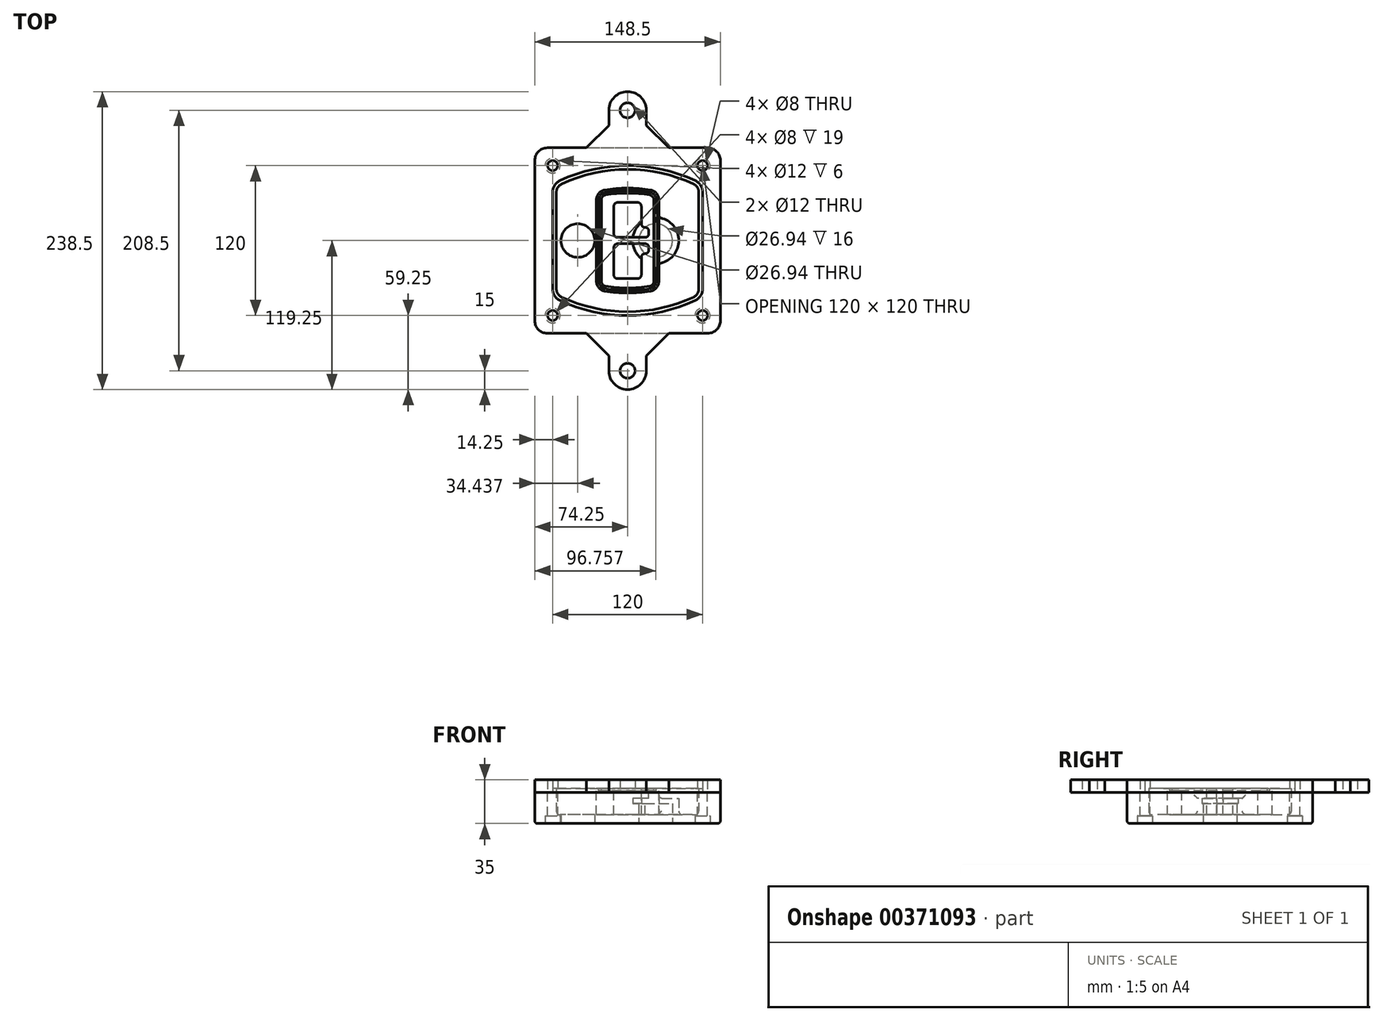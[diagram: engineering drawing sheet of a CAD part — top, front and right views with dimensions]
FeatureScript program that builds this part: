
annotation { "Feature Type Name" : "Feature", "Feature Type Description" : "" }
export const myFeature = defineFeature(function(context is Context, id is Id, definition is map)
    precondition{}
    {
        {
            var Q0;
            Q0=qCreatedBy(makeId("Top.planeOp"),FACE);
            var sketch = newSketch(context, id + "F0", { "sketchPlane" : qUnion([Q0])});
            skPoint(sketch, "E0.rect.middle", {"position": v(0, 0) * mm});
            skLineSegment(sketch, "E1.bottom", {"start": v(-64.25, -74.25) * mm, "end": v(64.25, -74.25) * mm});
            skLineSegment(sketch, "E1.top", {"start": v(-64.25, 74.25) * mm, "end": v(64.25, 74.25) * mm});
            skLineSegment(sketch, "E1.left", {"start": v(-74.25, -64.25) * mm, "end": v(-74.25, 64.25) * mm});
            skLineSegment(sketch, "E1.right", {"start": v(74.25, -64.25) * mm, "end": v(74.25, 64.25) * mm});
            skLineSegment(sketch, "E2", {"start": v(-74.25, 74.25) * mm, "end": v(74.25, -74.25) * mm, "construction": true});
            skLineSegment(sketch, "E3", {"start": v(74.25, 74.25) * mm, "end": v(-74.25, -74.25) * mm, "construction": true});
            skCircle(sketch, "E4", {"center": v(-60, 60) * mm, "radius": 4 * mm});
            skCircle(sketch, "E5", {"center": v(60, 60) * mm, "radius": 4 * mm});
            skCircle(sketch, "E6", {"center": v(60, -60) * mm, "radius": 4 * mm});
            skCircle(sketch, "E7", {"center": v(-60, -60) * mm, "radius": 4 * mm});
            skLineSegment(sketch, "E8", {"start": v(-60, 60) * mm, "end": v(60, 60) * mm, "construction": true});
            skLineSegment(sketch, "E9", {"start": v(60, 60) * mm, "end": v(60, -60) * mm, "construction": true});
            skLineSegment(sketch, "E10", {"start": v(60, -60) * mm, "end": v(-60, -60) * mm, "construction": true});
            skLineSegment(sketch, "E11", {"start": v(-60, -60) * mm, "end": v(-60, 60) * mm, "construction": true});
            skLineSegment(sketch, "E12", {"start": v(-60, 38.83) * mm, "end": v(-60, -38.83) * mm});
            skLineSegment(sketch, "E13", {"start": v(60, 38.83) * mm, "end": v(60, -38.83) * mm});
            skArc(sketch, "E14", {"start": v(54.26, 47.88) * mm, "mid": v(0, 60) * mm, "end": v(-54.26, 47.88) * mm});
            skArc(sketch, "E15", {"start": v(-54.26, -47.88) * mm, "mid": v(0, -60) * mm, "end": v(54.26, -47.88) * mm});
            skLineSegment(sketch, "E16", {"start": v(-60, 0) * mm, "end": v(60, 0) * mm, "construction": true});
            skPoint(sketch, "E17.visualSharp", {"position": v(-60, -45) * mm});
            skArc(sketch, "E17.filletArc", {"start": v(-60, -38.83) * mm, "mid": v(-58.44, -44.2) * mm, "end": v(-54.26, -47.88) * mm});
            skPoint(sketch, "E18.visualSharp", {"position": v(-60, 45) * mm});
            skArc(sketch, "E18.filletArc", {"start": v(-54.26, 47.88) * mm, "mid": v(-58.44, 44.2) * mm, "end": v(-60, 38.83) * mm});
            skPoint(sketch, "E19.visualSharp", {"position": v(60, 45) * mm});
            skArc(sketch, "E19.filletArc", {"start": v(60, 38.83) * mm, "mid": v(58.44, 44.2) * mm, "end": v(54.26, 47.88) * mm});
            skPoint(sketch, "E20.visualSharp", {"position": v(60, -45) * mm});
            skArc(sketch, "E20.filletArc", {"start": v(54.26, -47.88) * mm, "mid": v(58.44, -44.2) * mm, "end": v(60, -38.83) * mm});
            skPoint(sketch, "E21.visualSharp", {"position": v(-74.25, 74.25) * mm});
            skArc(sketch, "E21.filletArc", {"start": v(-64.25, 74.25) * mm, "mid": v(-71.32, 71.32) * mm, "end": v(-74.25, 64.25) * mm});
            skPoint(sketch, "E22.visualSharp", {"position": v(74.25, 74.25) * mm});
            skArc(sketch, "E22.filletArc", {"start": v(74.25, 64.25) * mm, "mid": v(71.32, 71.32) * mm, "end": v(64.25, 74.25) * mm});
            skPoint(sketch, "E23.visualSharp", {"position": v(74.25, -74.25) * mm});
            skArc(sketch, "E23.filletArc", {"start": v(64.25, -74.25) * mm, "mid": v(71.32, -71.32) * mm, "end": v(74.25, -64.25) * mm});
            skPoint(sketch, "E24.visualSharp", {"position": v(-74.25, -74.25) * mm});
            skArc(sketch, "E24.filletArc", {"start": v(-74.25, -64.25) * mm, "mid": v(-71.32, -71.32) * mm, "end": v(-64.25, -74.25) * mm});
            skArc(sketch, "E25.0", {"start": v(57, 38.83) * mm, "mid": v(55.9, 42.58) * mm, "end": v(52.98, 45.17) * mm});
            skLineSegment(sketch, "E25.1", {"start": v(57, 38.83) * mm, "end": v(57, -38.83) * mm});
            skArc(sketch, "E25.2", {"start": v(52.98, -45.17) * mm, "mid": v(55.9, -42.58) * mm, "end": v(57, -38.83) * mm});
            skArc(sketch, "E25.3", {"start": v(-52.98, -45.17) * mm, "mid": v(0, -57) * mm, "end": v(52.98, -45.17) * mm});
            skArc(sketch, "E25.4", {"start": v(-57, -38.83) * mm, "mid": v(-55.9, -42.58) * mm, "end": v(-52.98, -45.17) * mm});
            skArc(sketch, "E25.5", {"start": v(52.98, 45.17) * mm, "mid": v(0, 57) * mm, "end": v(-52.98, 45.17) * mm});
            skLineSegment(sketch, "E25.6", {"start": v(-57, 38.83) * mm, "end": v(-57, -38.83) * mm});
            skArc(sketch, "E25.7", {"start": v(-52.98, 45.17) * mm, "mid": v(-55.9, 42.58) * mm, "end": v(-57, 38.83) * mm});
            skArc(sketch, "E26.0", {"start": v(-55.96, 51.5) * mm, "mid": v(-61.82, 46.33) * mm, "end": v(-64, 38.83) * mm});
            skArc(sketch, "E26.1", {"start": v(55.96, 51.5) * mm, "mid": v(0, 64) * mm, "end": v(-55.96, 51.5) * mm});
            skArc(sketch, "E26.2", {"start": v(64, 38.83) * mm, "mid": v(61.82, 46.33) * mm, "end": v(55.96, 51.5) * mm});
            skLineSegment(sketch, "E26.3", {"start": v(64, 38.83) * mm, "end": v(64, -38.83) * mm});
            skArc(sketch, "E26.4", {"start": v(55.96, -51.5) * mm, "mid": v(61.82, -46.33) * mm, "end": v(64, -38.83) * mm});
            skLineSegment(sketch, "E26.5", {"start": v(-64, 38.83) * mm, "end": v(-64, -38.83) * mm});
            skArc(sketch, "E26.6", {"start": v(-55.96, -51.5) * mm, "mid": v(0, -64) * mm, "end": v(55.96, -51.5) * mm});
            skArc(sketch, "E26.7", {"start": v(-64, -38.83) * mm, "mid": v(-61.82, -46.33) * mm, "end": v(-55.96, -51.5) * mm});
            skSolve(sketch);
        }
        {
            var Q0;
            Q0=makeQuery(id+"F0.imprint","IMPRINT",FACE,{"disambiguationData":[TD([[makeQuery(id+"F0.imprint","IMPRINT",EDGE,{"derivedFrom":sQuery(id+"F0.wireOp",EDGE,"E1.bottom")}),1.0]])]});
            var Q1;
            Q1=makeQuery(id+"F0.imprint","IMPRINT",FACE,{"disambiguationData":[TD([[makeQuery(id+"F0.imprint","IMPRINT",EDGE,{"derivedFrom":sQuery(id+"F0.wireOp",EDGE,"E12")}),1.0]])]});
            var Q2;
            Q2=makeQuery(id+"F0.imprint","IMPRINT",FACE,{"disambiguationData":[TD([[makeQuery(id+"F0.imprint","IMPRINT",EDGE,{"derivedFrom":sQuery(id+"F0.wireOp",EDGE,"E25.0")}),1.0]])]});
            var Q3;
            Q3=makeQuery(id+"F0.imprint","IMPRINT",FACE,{"disambiguationData":[TD([[makeQuery(id+"F0.imprint","IMPRINT",EDGE,{"derivedFrom":sQuery(id+"F0.wireOp",EDGE,"E12")}),-1.0]])]});
            extrude(context, id + "F1", {"entities" : qUnion([Q0, Q1, Q2, Q3]), "oppositeDirection" : true, "depth" : 25 * mm});
        }
        {
            var Q0;
            Q0=makeQuery(id+"F0.imprint","IMPRINT",FACE,{"disambiguationData":[TD([[makeQuery(id+"F0.imprint","IMPRINT",EDGE,{"derivedFrom":sQuery(id+"F0.wireOp",EDGE,"E12")}),1.0]])]});
            extrude(context, id + "F2", {"entities" : qUnion([Q0]), "operationType" : NewBodyOperationType.ADD, "depth" : 3 * mm});
        }
        {
            var Q0;
            Q0=makeQuery(id+"F0.imprint","IMPRINT",FACE,{"disambiguationData":[TD([[makeQuery(id+"F0.imprint","IMPRINT",EDGE,{"derivedFrom":sQuery(id+"F0.wireOp",EDGE,"E25.0")}),1.0]])]});
            extrude(context, id + "F3", {"entities" : qUnion([Q0]), "operationType" : NewBodyOperationType.REMOVE, "oppositeDirection" : true, "depth" : 18 * mm});
        }
        {
            var Q0;
            Q0=makeQuery(id+"F2.opExtrude","CAP_FACE",FACE,{"disambiguationData":[OSD([sQuery(id+"F0.wireOp",EDGE,"E12"),sQuery(id+"F0.wireOp",EDGE,"E13"),sQuery(id+"F0.wireOp",EDGE,"E14"),sQuery(id+"F0.wireOp",EDGE,"E15"),sQuery(id+"F0.wireOp",EDGE,"E17.filletArc"),sQuery(id+"F0.wireOp",EDGE,"E18.filletArc"),sQuery(id+"F0.wireOp",EDGE,"E19.filletArc"),sQuery(id+"F0.wireOp",EDGE,"E20.filletArc"),sQuery(id+"F0.wireOp",EDGE,"E25.0"),sQuery(id+"F0.wireOp",EDGE,"E25.1"),sQuery(id+"F0.wireOp",EDGE,"E25.2"),sQuery(id+"F0.wireOp",EDGE,"E25.3"),sQuery(id+"F0.wireOp",EDGE,"E25.4"),sQuery(id+"F0.wireOp",EDGE,"E25.5"),sQuery(id+"F0.wireOp",EDGE,"E25.6"),sQuery(id+"F0.wireOp",EDGE,"E25.7")])],"isStart":false});
            var sketch = newSketch(context, id + "F4", { "sketchPlane" : qUnion([Q0])});
            skArc(sketch, "E27.0", {"start": v(-18.34, -40.45) * mm, "mid": v(0, -42) * mm, "end": v(18.34, -40.45) * mm});
            skArc(sketch, "E28.0", {"start": v(18.34, 40.45) * mm, "mid": v(0, 42) * mm, "end": v(-18.34, 40.45) * mm});
            skLineSegment(sketch, "E29", {"start": v(-25, 32.57) * mm, "end": v(-25, -32.57) * mm});
            skLineSegment(sketch, "E30", {"start": v(25, 32.57) * mm, "end": v(25, -32.57) * mm});
            skLineSegment(sketch, "E31", {"start": v(-25, 39.1) * mm, "end": v(25, 39.1) * mm, "construction": true});
            skLineSegment(sketch, "E32", {"start": v(-25, -39.1) * mm, "end": v(25, -39.1) * mm, "construction": true});
            skPoint(sketch, "E33.visualSharp", {"position": v(-25, 39.1) * mm});
            skArc(sketch, "E33.filletArc", {"start": v(-18.34, 40.45) * mm, "mid": v(-23.11, 37.73) * mm, "end": v(-25, 32.57) * mm});
            skPoint(sketch, "E34.visualSharp", {"position": v(25, 39.1) * mm});
            skArc(sketch, "E34.filletArc", {"start": v(25, 32.57) * mm, "mid": v(23.11, 37.73) * mm, "end": v(18.34, 40.45) * mm});
            skPoint(sketch, "E35.visualSharp", {"position": v(25, -39.1) * mm});
            skArc(sketch, "E35.filletArc", {"start": v(18.34, -40.45) * mm, "mid": v(23.11, -37.73) * mm, "end": v(25, -32.57) * mm});
            skPoint(sketch, "E36.visualSharp", {"position": v(-25, -39.1) * mm});
            skArc(sketch, "E36.filletArc", {"start": v(-25, -32.57) * mm, "mid": v(-23.11, -37.73) * mm, "end": v(-18.34, -40.45) * mm});
            skArc(sketch, "E37.0", {"start": v(52.98, 45.17) * mm, "mid": v(0, 57) * mm, "end": v(-52.98, 45.17) * mm});
            skArc(sketch, "E37.1", {"start": v(-52.98, 45.17) * mm, "mid": v(-55.9, 42.58) * mm, "end": v(-57, 38.83) * mm});
            skLineSegment(sketch, "E37.2", {"start": v(-57, 38.83) * mm, "end": v(-57, -38.83) * mm});
            skArc(sketch, "E37.3", {"start": v(-57, -38.83) * mm, "mid": v(-55.9, -42.58) * mm, "end": v(-52.98, -45.17) * mm});
            skArc(sketch, "E37.4", {"start": v(-52.98, -45.17) * mm, "mid": v(0, -57) * mm, "end": v(52.98, -45.17) * mm});
            skArc(sketch, "E37.5", {"start": v(52.98, -45.17) * mm, "mid": v(55.9, -42.58) * mm, "end": v(57, -38.83) * mm});
            skLineSegment(sketch, "E37.6", {"start": v(57, 38.83) * mm, "end": v(57, -38.83) * mm});
            skArc(sketch, "E37.7", {"start": v(57, 38.83) * mm, "mid": v(55.9, 42.58) * mm, "end": v(52.98, 45.17) * mm});
            skLineSegment(sketch, "E38.0", {"start": v(23, 32.57) * mm, "end": v(23, -32.57) * mm});
            skArc(sketch, "E38.1", {"start": v(18, -38.48) * mm, "mid": v(21.58, -36.44) * mm, "end": v(23, -32.57) * mm});
            skArc(sketch, "E38.2", {"start": v(-18, -38.48) * mm, "mid": v(0, -40) * mm, "end": v(18, -38.48) * mm});
            skArc(sketch, "E38.3", {"start": v(-23, -32.57) * mm, "mid": v(-21.58, -36.44) * mm, "end": v(-18, -38.48) * mm});
            skLineSegment(sketch, "E38.4", {"start": v(-23, 32.57) * mm, "end": v(-23, -32.57) * mm});
            skArc(sketch, "E38.5", {"start": v(23, 32.57) * mm, "mid": v(21.58, 36.44) * mm, "end": v(18, 38.48) * mm});
            skArc(sketch, "E38.6", {"start": v(-18, 38.48) * mm, "mid": v(-21.58, 36.44) * mm, "end": v(-23, 32.57) * mm});
            skArc(sketch, "E38.7", {"start": v(18, 38.48) * mm, "mid": v(0, 40) * mm, "end": v(-18, 38.48) * mm});
            skArc(sketch, "E39.0", {"start": v(21, 32.57) * mm, "mid": v(20.06, 35.15) * mm, "end": v(17.67, 36.5) * mm});
            skLineSegment(sketch, "E39.1", {"start": v(21, 32.57) * mm, "end": v(21, -32.57) * mm});
            skArc(sketch, "E39.2", {"start": v(17.67, -36.5) * mm, "mid": v(20.06, -35.15) * mm, "end": v(21, -32.57) * mm});
            skArc(sketch, "E39.3", {"start": v(-17.67, -36.5) * mm, "mid": v(0, -38) * mm, "end": v(17.67, -36.5) * mm});
            skArc(sketch, "E39.4", {"start": v(-21, -32.57) * mm, "mid": v(-20.06, -35.15) * mm, "end": v(-17.67, -36.5) * mm});
            skArc(sketch, "E39.5", {"start": v(17.67, 36.5) * mm, "mid": v(0, 38) * mm, "end": v(-17.67, 36.5) * mm});
            skLineSegment(sketch, "E39.6", {"start": v(-21, 32.57) * mm, "end": v(-21, -32.57) * mm});
            skArc(sketch, "E39.7", {"start": v(-17.67, 36.5) * mm, "mid": v(-20.06, 35.15) * mm, "end": v(-21, 32.57) * mm});
            skLineSegment(sketch, "E40", {"start": v(-25, 0) * mm, "end": v(25, 0) * mm, "construction": true});
            skLineSegment(sketch, "E41", {"start": v(-11, 5.5) * mm, "end": v(-11, 27.5) * mm});
            skLineSegment(sketch, "E42", {"start": v(-8, 30.5) * mm, "end": v(8, 30.5) * mm});
            skLineSegment(sketch, "E43", {"start": v(11, 27.5) * mm, "end": v(11, 13.5) * mm});
            skLineSegment(sketch, "E44", {"start": v(14, 10.5) * mm, "end": v(14, 10.5) * mm});
            skLineSegment(sketch, "E45", {"start": v(17, 7.5) * mm, "end": v(17, 5.5) * mm});
            skLineSegment(sketch, "E46", {"start": v(14, 2.5) * mm, "end": v(-8, 2.5) * mm});
            skPoint(sketch, "E47.visualSharp", {"position": v(-11, 30.5) * mm});
            skArc(sketch, "E47.filletArc", {"start": v(-8, 30.5) * mm, "mid": v(-10.12, 29.62) * mm, "end": v(-11, 27.5) * mm});
            skPoint(sketch, "E48.visualSharp", {"position": v(11, 30.5) * mm});
            skArc(sketch, "E48.filletArc", {"start": v(11, 27.5) * mm, "mid": v(10.12, 29.62) * mm, "end": v(8, 30.5) * mm});
            skPoint(sketch, "E49.visualSharp", {"position": v(11, 10.5) * mm});
            skArc(sketch, "E49.filletArc", {"start": v(11, 13.5) * mm, "mid": v(11.88, 11.38) * mm, "end": v(14, 10.5) * mm});
            skPoint(sketch, "E50.visualSharp", {"position": v(17, 10.5) * mm});
            skArc(sketch, "E50.filletArc", {"start": v(17, 7.5) * mm, "mid": v(16.12, 9.62) * mm, "end": v(14, 10.5) * mm});
            skPoint(sketch, "E51.visualSharp", {"position": v(17, 2.5) * mm});
            skArc(sketch, "E51.filletArc", {"start": v(14, 2.5) * mm, "mid": v(16.12, 3.38) * mm, "end": v(17, 5.5) * mm});
            skPoint(sketch, "E52.visualSharp", {"position": v(-11, 2.5) * mm});
            skArc(sketch, "E52.filletArc", {"start": v(-11, 5.5) * mm, "mid": v(-10.12, 3.38) * mm, "end": v(-8, 2.5) * mm});
            skLineSegment(sketch, "E53.0.MirrorCS", {"start": v(14, -2.5) * mm, "end": v(-8, -2.5) * mm});
            skArc(sketch, "E54.0.MirrorCS", {"start": v(-11, -5.5) * mm, "mid": v(-10.12, -3.38) * mm, "end": v(-8, -2.5) * mm});
            skLineSegment(sketch, "E55.0.MirrorCS", {"start": v(-11, -5.5) * mm, "end": v(-11, -27.5) * mm});
            skArc(sketch, "E56.0.MirrorCS", {"start": v(-8, -30.5) * mm, "mid": v(-10.12, -29.62) * mm, "end": v(-11, -27.5) * mm});
            skLineSegment(sketch, "E57.0.MirrorCS", {"start": v(-8, -30.5) * mm, "end": v(8, -30.5) * mm});
            skArc(sketch, "E58.0.MirrorCS", {"start": v(11, -27.5) * mm, "mid": v(10.12, -29.62) * mm, "end": v(8, -30.5) * mm});
            skLineSegment(sketch, "E59.0.MirrorCS", {"start": v(11, -27.5) * mm, "end": v(11, -13.5) * mm});
            skArc(sketch, "E60.0.MirrorCS", {"start": v(11, -13.5) * mm, "mid": v(11.88, -11.38) * mm, "end": v(14, -10.5) * mm});
            skArc(sketch, "E61.0.MirrorCS", {"start": v(17, -7.5) * mm, "mid": v(16.12, -9.62) * mm, "end": v(14, -10.5) * mm});
            skLineSegment(sketch, "E62.0.MirrorCS", {"start": v(17, -7.5) * mm, "end": v(17, -5.5) * mm});
            skArc(sketch, "E63.0.MirrorCS", {"start": v(14, -2.5) * mm, "mid": v(16.12, -3.38) * mm, "end": v(17, -5.5) * mm});
            skSolve(sketch);
        }
        {
            var Q0;
            Q0=makeQuery(id+"F4.imprint","IMPRINT",FACE,{"disambiguationData":[TD([[makeQuery(id+"F4.imprint","IMPRINT",EDGE,{"derivedFrom":sQuery(id+"F4.wireOp",EDGE,"E27.0")}),1.0]])]});
            var Q1;
            Q1=makeQuery(id+"F4.imprint","IMPRINT",FACE,{"disambiguationData":[TD([[makeQuery(id+"F4.imprint","IMPRINT",EDGE,{"derivedFrom":sQuery(id+"F4.wireOp",EDGE,"E38.0")}),-1.0]])]});
            var Q2;
            Q2=makeQuery(id+"F4.imprint","IMPRINT",FACE,{"disambiguationData":[TD([[makeQuery(id+"F4.imprint","IMPRINT",EDGE,{"derivedFrom":sQuery(id+"F4.wireOp",EDGE,"E39.0")}),1.0]])]});
            extrude(context, id + "F5", {"entities" : qUnion([Q0, Q1, Q2]), "operationType" : NewBodyOperationType.ADD, "endBound" : BoundingType.UP_TO_NEXT, "oppositeDirection" : true, "depth" : 25 * mm});
        }
        {
            var Q0;
            Q0=makeQuery(id+"F4.imprint","IMPRINT",FACE,{"disambiguationData":[TD([[makeQuery(id+"F4.imprint","IMPRINT",EDGE,{"derivedFrom":sQuery(id+"F4.wireOp",EDGE,"E38.0")}),-1.0]])]});
            extrude(context, id + "F6", {"entities" : qUnion([Q0]), "operationType" : NewBodyOperationType.REMOVE, "oppositeDirection" : true, "depth" : 2 * mm});
        }
        {
            var Q0;
            Q0=makeQuery(id+"F1.opExtrude","CAP_FACE",FACE,{"disambiguationData":[OSD([sQuery(id+"F0.wireOp",EDGE,"E1.bottom"),sQuery(id+"F0.wireOp",EDGE,"E1.top"),sQuery(id+"F0.wireOp",EDGE,"E1.left"),sQuery(id+"F0.wireOp",EDGE,"E1.right"),sQuery(id+"F0.wireOp",EDGE,"E4"),sQuery(id+"F0.wireOp",EDGE,"E5"),sQuery(id+"F0.wireOp",EDGE,"E6"),sQuery(id+"F0.wireOp",EDGE,"E7"),sQuery(id+"F0.wireOp",EDGE,"E21.filletArc"),sQuery(id+"F0.wireOp",EDGE,"E22.filletArc"),sQuery(id+"F0.wireOp",EDGE,"E23.filletArc"),sQuery(id+"F0.wireOp",EDGE,"E24.filletArc")])],"isStart":false});
            var sketch = newSketch(context, id + "F7", { "sketchPlane" : qUnion([Q0])});
            skCircle(sketch, "E64", {"center": v(22.5, 0) * mm, "radius": 13.47 * mm});
            skCircle(sketch, "E65", {"center": v(-39.81, 0) * mm, "radius": 13.47 * mm});
            skLineSegment(sketch, "E66", {"start": v(74.25, 0) * mm, "end": v(-74.25, 0) * mm});
            skCircle(sketch, "E67", {"center": v(22.5, 0) * mm, "radius": 18.47 * mm});
            skCircle(sketch, "E68", {"center": v(60, -60) * mm, "radius": 6 * mm});
            skCircle(sketch, "E69", {"center": v(-60, -60) * mm, "radius": 6 * mm});
            skCircle(sketch, "E70", {"center": v(-60, 60) * mm, "radius": 6 * mm});
            skCircle(sketch, "E71", {"center": v(60, 60) * mm, "radius": 6 * mm});
            skSolve(sketch);
        }
        {
            var Q0;
            {var subQ1=sQuery(id+"F7.wireOp",EDGE,"E66");var subQ4=sQuery(id+"F7.wireOp",EDGE,"E64");var subQ6=makeQuery(id+"F7.imprint","INTERSECT",VERTEX,{"disambiguationData":[OD(0.0)],"derivedFrom":[subQ4,subQ1]});Q0=makeQuery(id+"F7.imprint","IMPRINT",FACE,{"disambiguationData":[TD([[makeQuery(id+"F7.imprint","IMPRINT",EDGE,{"disambiguationData":[TD([[subQ6,-1.0]])],"derivedFrom":subQ4}),-1.0]])]});}
            var Q1;
            {var subQ0=sQuery(id+"F7.wireOp",EDGE,"E66");var subQ1=sQuery(id+"F7.wireOp",EDGE,"E64");var subQ3=makeQuery(id+"F7.imprint","INTERSECT",VERTEX,{"disambiguationData":[OD(0.0)],"derivedFrom":[subQ1,subQ0]});Q1=makeQuery(id+"F7.imprint","IMPRINT",FACE,{"disambiguationData":[TD([[makeQuery(id+"F7.imprint","IMPRINT",EDGE,{"disambiguationData":[TD([[subQ3,-1.0]])],"derivedFrom":subQ1}),1.0]])]});}
            var Q2;
            {var subQ0=sQuery(id+"F7.wireOp",EDGE,"E66");var subQ1=sQuery(id+"F7.wireOp",EDGE,"E64");var subQ3=makeQuery(id+"F7.imprint","INTERSECT",VERTEX,{"disambiguationData":[OD(0.0)],"derivedFrom":[subQ1,subQ0]});Q2=makeQuery(id+"F7.imprint","IMPRINT",FACE,{"disambiguationData":[TD([[makeQuery(id+"F7.imprint","IMPRINT",EDGE,{"disambiguationData":[TD([[subQ3,1.0]])],"derivedFrom":subQ1}),1.0]])]});}
            var Q3;
            {var subQ1=sQuery(id+"F7.wireOp",EDGE,"E66");var subQ4=sQuery(id+"F7.wireOp",EDGE,"E64");var subQ6=makeQuery(id+"F7.imprint","INTERSECT",VERTEX,{"disambiguationData":[OD(0.0)],"derivedFrom":[subQ4,subQ1]});Q3=makeQuery(id+"F7.imprint","IMPRINT",FACE,{"disambiguationData":[TD([[makeQuery(id+"F7.imprint","IMPRINT",EDGE,{"disambiguationData":[TD([[subQ6,1.0]])],"derivedFrom":subQ4}),-1.0]])]});}
            extrude(context, id + "F8", {"entities" : qUnion([Q0, Q1, Q2, Q3]), "operationType" : NewBodyOperationType.ADD, "oppositeDirection" : true, "depth" : 20 * mm});
        }
        {
            var Q0;
            {var subQ0=sQuery(id+"F7.wireOp",EDGE,"E66");var subQ1=sQuery(id+"F7.wireOp",EDGE,"E64");var subQ3=makeQuery(id+"F7.imprint","INTERSECT",VERTEX,{"disambiguationData":[OD(0.0)],"derivedFrom":[subQ1,subQ0]});Q0=makeQuery(id+"F7.imprint","IMPRINT",FACE,{"disambiguationData":[TD([[makeQuery(id+"F7.imprint","IMPRINT",EDGE,{"disambiguationData":[TD([[subQ3,-1.0]])],"derivedFrom":subQ1}),1.0]])]});}
            var Q1;
            {var subQ0=sQuery(id+"F7.wireOp",EDGE,"E66");var subQ1=sQuery(id+"F7.wireOp",EDGE,"E64");var subQ3=makeQuery(id+"F7.imprint","INTERSECT",VERTEX,{"disambiguationData":[OD(0.0)],"derivedFrom":[subQ1,subQ0]});Q1=makeQuery(id+"F7.imprint","IMPRINT",FACE,{"disambiguationData":[TD([[makeQuery(id+"F7.imprint","IMPRINT",EDGE,{"disambiguationData":[TD([[subQ3,1.0]])],"derivedFrom":subQ1}),1.0]])]});}
            extrude(context, id + "F9", {"entities" : qUnion([Q0, Q1]), "operationType" : NewBodyOperationType.REMOVE, "oppositeDirection" : true, "depth" : 16 * mm});
        }
        {
            var Q0;
            {var subQ0=sQuery(id+"F7.wireOp",EDGE,"E66");var subQ1=sQuery(id+"F7.wireOp",EDGE,"E65");var subQ3=makeQuery(id+"F7.imprint","INTERSECT",VERTEX,{"disambiguationData":[OD(0.0)],"derivedFrom":[subQ1,subQ0]});Q0=makeQuery(id+"F7.imprint","IMPRINT",FACE,{"disambiguationData":[TD([[makeQuery(id+"F7.imprint","IMPRINT",EDGE,{"disambiguationData":[TD([[subQ3,-1.0]])],"derivedFrom":subQ1}),1.0]])]});}
            var Q1;
            {var subQ0=sQuery(id+"F7.wireOp",EDGE,"E66");var subQ1=sQuery(id+"F7.wireOp",EDGE,"E65");var subQ3=makeQuery(id+"F7.imprint","INTERSECT",VERTEX,{"disambiguationData":[OD(0.0)],"derivedFrom":[subQ1,subQ0]});Q1=makeQuery(id+"F7.imprint","IMPRINT",FACE,{"disambiguationData":[TD([[makeQuery(id+"F7.imprint","IMPRINT",EDGE,{"disambiguationData":[TD([[subQ3,1.0]])],"derivedFrom":subQ1}),1.0]])]});}
            extrude(context, id + "F10", {"entities" : qUnion([Q0, Q1]), "operationType" : NewBodyOperationType.REMOVE, "oppositeDirection" : true, "depth" : 25 * mm});
        }
        {
            var Q0;
            Q0=makeQuery(id+"F7.imprint","IMPRINT",FACE,{"disambiguationData":[TD([[makeQuery(id+"F7.imprint","IMPRINT",EDGE,{"derivedFrom":sQuery(id+"F7.wireOp",EDGE,"E68")}),1.0]])]});
            var Q1;
            Q1=makeQuery(id+"F7.imprint","IMPRINT",FACE,{"disambiguationData":[TD([[makeQuery(id+"F7.imprint","IMPRINT",EDGE,{"derivedFrom":makeQuery(id+"F1.opExtrude","CAP_EDGE",EDGE,{"disambiguationData":[OSD([sQuery(id+"F0.wireOp",EDGE,"E5")])],"isStart":false})}),-1.0]])]});
            var Q2;
            Q2=makeQuery(id+"F7.imprint","IMPRINT",FACE,{"disambiguationData":[TD([[makeQuery(id+"F7.imprint","IMPRINT",EDGE,{"derivedFrom":sQuery(id+"F7.wireOp",EDGE,"E69")}),1.0]])]});
            var Q3;
            Q3=makeQuery(id+"F7.imprint","IMPRINT",FACE,{"disambiguationData":[TD([[makeQuery(id+"F7.imprint","IMPRINT",EDGE,{"derivedFrom":makeQuery(id+"F1.opExtrude","CAP_EDGE",EDGE,{"disambiguationData":[OSD([sQuery(id+"F0.wireOp",EDGE,"E4")])],"isStart":false})}),-1.0]])]});
            var Q4;
            Q4=makeQuery(id+"F7.imprint","IMPRINT",FACE,{"disambiguationData":[TD([[makeQuery(id+"F7.imprint","IMPRINT",EDGE,{"derivedFrom":sQuery(id+"F7.wireOp",EDGE,"E70")}),1.0]])]});
            var Q5;
            Q5=makeQuery(id+"F7.imprint","IMPRINT",FACE,{"disambiguationData":[TD([[makeQuery(id+"F7.imprint","IMPRINT",EDGE,{"derivedFrom":makeQuery(id+"F1.opExtrude","CAP_EDGE",EDGE,{"disambiguationData":[OSD([sQuery(id+"F0.wireOp",EDGE,"E7")])],"isStart":false})}),-1.0]])]});
            var Q6;
            Q6=makeQuery(id+"F7.imprint","IMPRINT",FACE,{"disambiguationData":[TD([[makeQuery(id+"F7.imprint","IMPRINT",EDGE,{"derivedFrom":sQuery(id+"F7.wireOp",EDGE,"E71")}),1.0]])]});
            var Q7;
            Q7=makeQuery(id+"F7.imprint","IMPRINT",FACE,{"disambiguationData":[TD([[makeQuery(id+"F7.imprint","IMPRINT",EDGE,{"derivedFrom":makeQuery(id+"F1.opExtrude","CAP_EDGE",EDGE,{"disambiguationData":[OSD([sQuery(id+"F0.wireOp",EDGE,"E6")])],"isStart":false})}),-1.0]])]});
            extrude(context, id + "F11", {"entities" : qUnion([Q0, Q1, Q2, Q3, Q4, Q5, Q6, Q7]), "operationType" : NewBodyOperationType.REMOVE, "oppositeDirection" : true, "depth" : 6 * mm});
        }
        {
            var Q0;
            Q0=makeQuery(id+"F9.boolean.opBoolean","COPY",FACE,{"derivedFrom":makeQuery(id+"F9.opExtrude","CAP_FACE",FACE,{"disambiguationData":[OSD([sQuery(id+"F7.wireOp",EDGE,"E64")])],"isStart":false})});
            var sketch = newSketch(context, id + "F12", { "sketchPlane" : qUnion([Q0])});
            skArc(sketch, "E72.0", {"start": v(11, 14.45) * mm, "mid": v(6.45, 9.13) * mm, "end": v(4.2, 2.5) * mm});
            skArc(sketch, "E72.1", {"start": v(4.2, -2.5) * mm, "mid": v(6.45, -9.13) * mm, "end": v(11, -14.45) * mm});
            skLineSegment(sketch, "E73", {"start": v(4.2, -2.5) * mm, "end": v(14, -2.5) * mm});
            skLineSegment(sketch, "E74.0", {"start": v(14, 2.5) * mm, "end": v(4.2, 2.5) * mm});
            skArc(sketch, "E74.1", {"start": v(14, 2.5) * mm, "mid": v(16.12, 3.38) * mm, "end": v(17, 5.5) * mm});
            skLineSegment(sketch, "E74.2", {"start": v(17, 7.5) * mm, "end": v(17, 5.5) * mm});
            skArc(sketch, "E74.3", {"start": v(17, 7.5) * mm, "mid": v(16.12, 9.62) * mm, "end": v(14, 10.5) * mm});
            skArc(sketch, "E74.4", {"start": v(11, 13.5) * mm, "mid": v(11.88, 11.38) * mm, "end": v(14, 10.5) * mm});
            skLineSegment(sketch, "E74.5", {"start": v(11, 14.45) * mm, "end": v(11, 13.5) * mm});
            skLineSegment(sketch, "E74.7", {"start": v(14, -2.5) * mm, "end": v(4.2, -2.5) * mm});
            skArc(sketch, "E74.8", {"start": v(14, -2.5) * mm, "mid": v(16.12, -3.38) * mm, "end": v(17, -5.5) * mm});
            skLineSegment(sketch, "E74.9", {"start": v(17, -7.5) * mm, "end": v(17, -5.5) * mm});
            skArc(sketch, "E74.10", {"start": v(17, -7.5) * mm, "mid": v(16.12, -9.62) * mm, "end": v(14, -10.5) * mm});
            skArc(sketch, "E74.11", {"start": v(11, -13.5) * mm, "mid": v(11.88, -11.38) * mm, "end": v(14, -10.5) * mm});
            skLineSegment(sketch, "E74.12", {"start": v(11, -14.45) * mm, "end": v(11, -13.5) * mm});
            skPoint(sketch, "E75.orphan", {"position": v(11, -27.5) * mm});
            skPoint(sketch, "E76.orphan", {"position": v(-8, -2.5) * mm});
            skPoint(sketch, "E77.orphan", {"position": v(-8, 2.5) * mm});
            skPoint(sketch, "E78.orphan", {"position": v(11, 27.5) * mm});
            skSolve(sketch);
        }
        {
            var Q0;
            {var subQ7=sQuery(id+"F12.wireOp",EDGE,"E72.0");var subQ14=sQuery(id+"F12.wireOp",EDGE,"E72.1");var subQ16=sQuery(id+"F12.wireOp",EDGE,"E74.1");var subQ18=sQuery(id+"F12.wireOp",EDGE,"E74.8");Q0=qUnion([makeQuery(id+"F12.imprint","IMPRINT",FACE,{"disambiguationData":[TD([[makeQuery(id+"F12.imprint","IMPRINT",EDGE,{"derivedFrom":subQ7}),1.0]])]}),makeQuery(id+"F12.imprint","IMPRINT",FACE,{"disambiguationData":[TD([[makeQuery(id+"F12.imprint","IMPRINT",EDGE,{"derivedFrom":subQ14}),1.0]])]}),makeQuery(id+"F12.imprint","IMPRINT",FACE,{"disambiguationData":[TD([[makeQuery(id+"F12.imprint","IMPRINT",EDGE,{"derivedFrom":subQ16}),1.0]])]}),makeQuery(id+"F12.imprint","IMPRINT",FACE,{"disambiguationData":[TD([[makeQuery(id+"F12.imprint","IMPRINT",EDGE,{"derivedFrom":subQ18}),-1.0]])]})]);}
            var Q1;
            Q1=makeQuery(id+"F5.boolean.opBoolean","SPLIT",FACE,{"disambiguationData":[TD([makeQuery(id+"F5.opExtrude","SWEPT_FACE",FACE,{"disambiguationData":[OSD([sQuery(id+"F4.wireOp",EDGE,"E41")])]})])],"derivedFrom":makeQuery(id+"F3.boolean.opBoolean","COPY",FACE,{"derivedFrom":makeQuery(id+"F3.opExtrude","CAP_FACE",FACE,{"disambiguationData":[OSD([sQuery(id+"F0.wireOp",EDGE,"E25.0"),sQuery(id+"F0.wireOp",EDGE,"E25.1"),sQuery(id+"F0.wireOp",EDGE,"E25.2"),sQuery(id+"F0.wireOp",EDGE,"E25.3"),sQuery(id+"F0.wireOp",EDGE,"E25.4"),sQuery(id+"F0.wireOp",EDGE,"E25.5"),sQuery(id+"F0.wireOp",EDGE,"E25.6"),sQuery(id+"F0.wireOp",EDGE,"E25.7")])],"isStart":false})})});
            extrude(context, id + "F13", {"entities" : qUnion([Q0]), "operationType" : NewBodyOperationType.REMOVE, "endBound" : BoundingType.UP_TO_SURFACE, "endBoundEntityFace" : qUnion([Q1]), "depth" : 25 * mm});
        }
        {
            var Q0;
            Q0=makeQuery(id+"F3.boolean.opBoolean","COPY",EDGE,{"derivedFrom":makeQuery(id+"F3.opExtrude","CAP_EDGE",EDGE,{"disambiguationData":[OSD([sQuery(id+"F0.wireOp",EDGE,"E25.6")])],"isStart":false})});
            var Q1;
            Q1=makeQuery(id+"F8.boolean.opBoolean","INTERSECT",EDGE,{"derivedFrom":[makeQuery(id+"F5.opExtrude","SWEPT_FACE",FACE,{"disambiguationData":[OSD([sQuery(id+"F4.wireOp",EDGE,"E30")])]}),makeQuery(id+"F8.opExtrude","CAP_FACE",FACE,{"disambiguationData":[OSD([sQuery(id+"F7.wireOp",EDGE,"E67")])],"isStart":false})]});
            var Q2;
            Q2=makeQuery(id+"F8.boolean.opBoolean","INTERSECT",EDGE,{"disambiguationData":[OD(1.0)],"derivedFrom":[makeQuery(id+"F5.opExtrude","SWEPT_FACE",FACE,{"disambiguationData":[OSD([sQuery(id+"F4.wireOp",EDGE,"E30")])]}),makeQuery(id+"F8.opExtrude","SWEPT_FACE",FACE,{"disambiguationData":[OSD([sQuery(id+"F7.wireOp",EDGE,"E67")])]})]});
            var Q3;
            {var subQ0=sQuery(id+"F4.wireOp",EDGE,"E30");Q3=makeQuery(id+"F8.boolean.opBoolean","SPLIT",EDGE,{"disambiguationData":[TD([makeQuery(id+"F5.opExtrude","SWEPT_FACE",FACE,{"disambiguationData":[OSD([sQuery(id+"F4.wireOp",EDGE,"E35.filletArc")])]})])],"derivedFrom":makeQuery(id+"F5.opExtrude","CAP_EDGE",EDGE,{"disambiguationData":[OSD([subQ0])],"isStart":false})});}
            var Q4;
            {var subQ0=sQuery(id+"F0.wireOp",EDGE,"E25.7");var subQ1=sQuery(id+"F0.wireOp",EDGE,"E25.1");var subQ2=sQuery(id+"F0.wireOp",EDGE,"E25.6");var subQ3=sQuery(id+"F0.wireOp",EDGE,"E25.5");var subQ4=sQuery(id+"F0.wireOp",EDGE,"E25.4");var subQ5=sQuery(id+"F0.wireOp",EDGE,"E25.0");var subQ6=sQuery(id+"F0.wireOp",EDGE,"E25.2");var subQ7=sQuery(id+"F0.wireOp",EDGE,"E25.3");Q4=makeQuery(id+"F8.boolean.opBoolean","INTERSECT",EDGE,{"derivedFrom":[makeQuery(id+"F5.boolean.opBoolean","SPLIT",FACE,{"disambiguationData":[TD([makeQuery(id+"F2.opExtrude","SWEPT_FACE",FACE,{"disambiguationData":[OSD([subQ5])]})])],"derivedFrom":makeQuery(id+"F3.boolean.opBoolean","COPY",FACE,{"derivedFrom":makeQuery(id+"F3.opExtrude","CAP_FACE",FACE,{"disambiguationData":[OSD([subQ5,subQ1,subQ6,subQ7,subQ4,subQ3,subQ2,subQ0])],"isStart":false})})}),makeQuery(id+"F8.opExtrude","SWEPT_FACE",FACE,{"disambiguationData":[OSD([sQuery(id+"F7.wireOp",EDGE,"E67")])]})]});}
            var Q5;
            Q5=makeQuery(id+"F8.boolean.opBoolean","INTERSECT",EDGE,{"disambiguationData":[OD(0.0)],"derivedFrom":[makeQuery(id+"F5.opExtrude","SWEPT_FACE",FACE,{"disambiguationData":[OSD([sQuery(id+"F4.wireOp",EDGE,"E30")])]}),makeQuery(id+"F8.opExtrude","SWEPT_FACE",FACE,{"disambiguationData":[OSD([sQuery(id+"F7.wireOp",EDGE,"E67")])]})]});
            fillet(context, id + "F14", {"entities" : qUnion([Q0, Q1, Q2, Q3, Q4, Q5]), "radius" : 3 * mm, "tangentPropagation" : true, "allowEdgeOverflow" : false});
        }
        {
            var Q0;
            Q0=makeQuery(id+"F1.opExtrude","CAP_EDGE",EDGE,{"disambiguationData":[OSD([sQuery(id+"F0.wireOp",EDGE,"E1.bottom")])],"isStart":false});
            fillet(context, id + "F15", {"entities" : qUnion([Q0]), "radius" : 2 * mm, "tangentPropagation" : true, "allowEdgeOverflow" : false});
        }
        {
            var Q0;
            {var subQ0=sQuery(id+"F0.wireOp",EDGE,"E21.filletArc");var subQ1=sQuery(id+"F0.wireOp",EDGE,"E7");var subQ2=sQuery(id+"F0.wireOp",EDGE,"E6");var subQ3=sQuery(id+"F0.wireOp",EDGE,"E5");var subQ4=sQuery(id+"F0.wireOp",EDGE,"E4");var subQ5=sQuery(id+"F0.wireOp",EDGE,"E22.filletArc");var subQ6=sQuery(id+"F0.wireOp",EDGE,"E1.bottom");var subQ7=sQuery(id+"F0.wireOp",EDGE,"E1.right");var subQ8=sQuery(id+"F0.wireOp",EDGE,"E1.top");var subQ9=sQuery(id+"F0.wireOp",EDGE,"E1.left");var subQ10=sQuery(id+"F0.wireOp",EDGE,"E23.filletArc");var subQ11=sQuery(id+"F0.wireOp",EDGE,"E24.filletArc");Q0=makeQuery(id+"F2.boolean.opBoolean","SPLIT",FACE,{"disambiguationData":[TD([makeQuery(id+"F1.opExtrude","SWEPT_FACE",FACE,{"disambiguationData":[OSD([subQ6])]})])],"derivedFrom":makeQuery(id+"F1.opExtrude","CAP_FACE",FACE,{"disambiguationData":[OSD([subQ6,subQ8,subQ9,subQ7,subQ4,subQ3,subQ2,subQ1,subQ0,subQ5,subQ10,subQ11])],"isStart":true})});}
            var sketch = newSketch(context, id + "F16", { "sketchPlane" : qUnion([Q0])});
            skCircle(sketch, "E79", {"center": v(0, 104.25) * mm, "radius": 6 * mm});
            skLineSegment(sketch, "E80", {"start": v(32.96, 74.25) * mm, "end": v(14.96, 92.25) * mm});
            skLineSegment(sketch, "E81", {"start": v(-33.04, 74.25) * mm, "end": v(-15.04, 92.25) * mm});
            skLineSegment(sketch, "E82", {"start": v(-15.04, 92.25) * mm, "end": v(-15.04, 104.46) * mm});
            skLineSegment(sketch, "E83", {"start": v(14.96, 92.25) * mm, "end": v(14.96, 104.46) * mm});
            skArc(sketch, "E84", {"start": v(14.96, 104.46) * mm, "mid": v(-0.04, 119.25) * mm, "end": v(-15.04, 104.46) * mm});
            skLineSegment(sketch, "E85", {"start": v(-74.25, 0) * mm, "end": v(74.25, 0) * mm});
            skLineSegment(sketch, "E86.MirrorCS", {"start": v(32.96, -74.25) * mm, "end": v(14.96, -92.25) * mm});
            skLineSegment(sketch, "E87.MirrorCS", {"start": v(14.96, -92.25) * mm, "end": v(14.96, -104.46) * mm});
            skArc(sketch, "E88.MirrorCS", {"start": v(14.96, -104.46) * mm, "mid": v(-0.04, -119.25) * mm, "end": v(-15.04, -104.46) * mm});
            skLineSegment(sketch, "E89.MirrorCS", {"start": v(-15.04, -92.25) * mm, "end": v(-15.04, -104.46) * mm});
            skLineSegment(sketch, "E90.MirrorCS", {"start": v(-33.04, -74.25) * mm, "end": v(-15.04, -92.25) * mm});
            skCircle(sketch, "E91.MirrorC", {"center": v(0, -104.25) * mm, "radius": 6 * mm});
            skSolve(sketch);
        }
        {
            var Q0;
            {var subQ0=sQuery(id+"F16.wireOp",EDGE,"E86.MirrorCS");Q0=makeQuery(id+"F16.imprint","IMPRINT",FACE,{"disambiguationData":[TD([[makeQuery(id+"F16.imprint","IMPRINT",EDGE,{"derivedFrom":subQ0}),-1.0]])]});}
            var Q1;
            Q1=makeQuery(id+"F16.imprint","IMPRINT",FACE,{"disambiguationData":[TD([[makeQuery(id+"F16.imprint","IMPRINT",EDGE,{"derivedFrom":sQuery(id+"F16.wireOp",EDGE,"E79")}),-1.0]])]});
            var Q2;
            Q2=makeQuery(id+"F16.imprint","IMPRINT",FACE,{"disambiguationData":[TD([[makeQuery(id+"F16.imprint","IMPRINT",EDGE,{"derivedFrom":makeQuery(id+"F1.opExtrude","CAP_EDGE",EDGE,{"disambiguationData":[OSD([sQuery(id+"F0.wireOp",EDGE,"E4")])],"isStart":true})}),-1.0]])]});
            var Q3;
            Q3=makeQuery(id+"F16.imprint","IMPRINT",FACE,{"disambiguationData":[TD([[makeQuery(id+"F16.imprint","IMPRINT",EDGE,{"derivedFrom":makeQuery(id+"F1.opExtrude","CAP_EDGE",EDGE,{"disambiguationData":[OSD([sQuery(id+"F0.wireOp",EDGE,"E6")])],"isStart":true})}),-1.0]])]});
            extrude(context, id + "F17", {"entities" : qUnion([Q0, Q1, Q2, Q3]), "depth" : 10 * mm});
        }
    });
